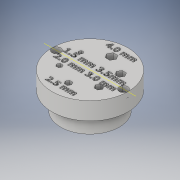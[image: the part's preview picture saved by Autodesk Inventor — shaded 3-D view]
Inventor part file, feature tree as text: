
AUTODESK INVENTOR PART (.ipt)
format: ipt  version: 2019.1 (Build 231200000, 200)  size: 931,840 bytes
history: native  units: in
note: dims shown in document units (in); Inventor stores cm internally (conversion verified against a paired STEP export)
features: sketch x5, extrude x4, hole x1
ambient origin geometry x8: Origin, YZ Plane, XZ Plane, XY Plane, X Axis, Y Axis, Z Axis, Center Point
bodies: Solid1 (feature_tree)
feature tree (10):
  extrude  "Extrusion1"  Depth=0.375in TaperAngle=0.0deg
  extrude  "Extrusion2"  Depth=0.375in TaperAngle=0.0deg
  hole  "Hole1"  [1 undecoded]
  extrude  "Extrusion4"  Depth=0.95in
  extrude  "Extrusion5"  Depth=0.1772in
  sketch  "Sketch1"  dims[d0=1.62in d1=0.375in d2=0.0in]
  sketch  "Sketch2"  dims[d3=1.25in d4=0.375in d5=0.0in]
  sketch  "Sketch4"  dims[d9=0.7175in d10=0.7175in]
  sketch  "Sketch5"  dims[d11=0.129in d12=0.75in d13=0.183in d14=0.112in d15=0.5635in d16=1.0in d17=0.8108in d18=0.95in]
  sketch  "Sketch6"  dims[d19=2.3622in d21=360.0deg d23=0.1772in d24=0.1575in d25=0.1378in d26=0.1181in d27=0.0984in d28=0.0787in d29=0.0in d30=0.0in d31=0.6in d32=0.05in d33=0.155in d34=0.125in d35=0.0in]
note: 1 required parameter value undecoded (feature->parameter linkage not recoverable at this tier; creation-order binding heuristic only, values carry confidence <= 0.55)
